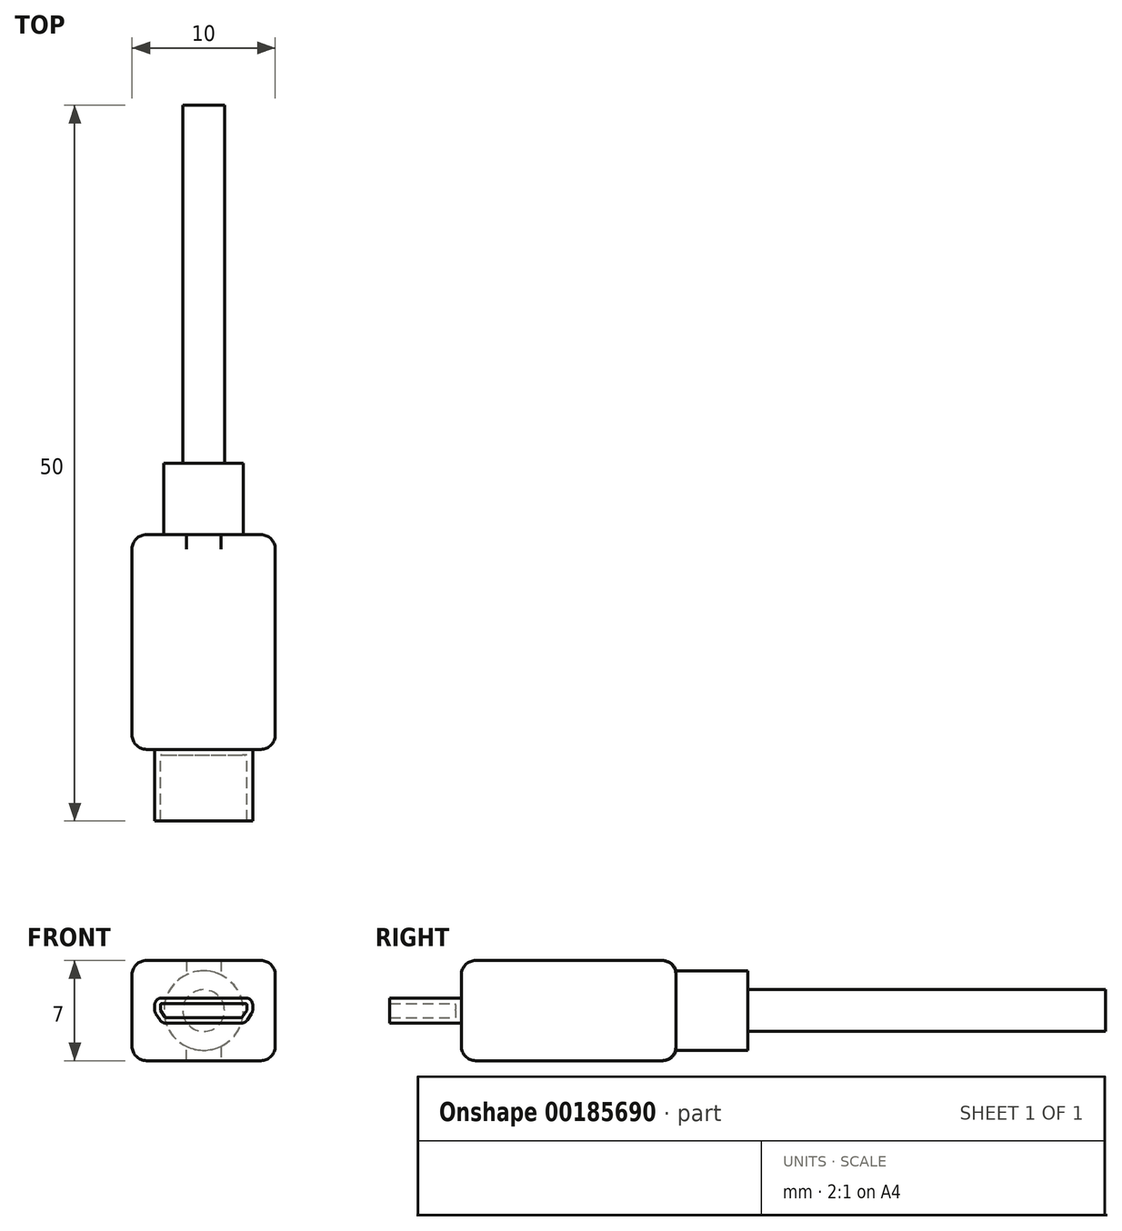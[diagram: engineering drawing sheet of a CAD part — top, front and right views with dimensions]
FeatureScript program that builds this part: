
annotation { "Feature Type Name" : "Feature", "Feature Type Description" : "" }
export const myFeature = defineFeature(function(context is Context, id is Id, definition is map)
    precondition{}
    {
        {
            var Q0;
            Q0=qCreatedBy(makeId("Front.planeOp"),FACE);
            var sketch = newSketch(context, id + "F0", { "sketchPlane" : qUnion([Q0])});
            skLineSegment(sketch, "E0.bottom", {"start": v(5, 3.5) * mm, "end": v(-5, 3.5) * mm});
            skLineSegment(sketch, "E0.top", {"start": v(5, -3.5) * mm, "end": v(-5, -3.5) * mm});
            skLineSegment(sketch, "E0.left", {"start": v(5, 3.5) * mm, "end": v(5, -3.5) * mm});
            skLineSegment(sketch, "E0.right", {"start": v(-5, 3.5) * mm, "end": v(-5, -3.5) * mm});
            skPoint(sketch, "E0.middle", {"position": v(0, 0) * mm});
            skSolve(sketch);
        }
        {
            var Q0;
            Q0=qSketchRegion(id+"F0",true);
            extrude(context, id + "F1", {"entities" : qUnion([Q0]), "oppositeDirection" : true, "depth" : 15 * mm});
        }
        {
            var Q0;
            Q0=makeQuery(id+"F1.opExtrude","CAP_FACE",FACE,{"disambiguationData":[OSD([sQuery(id+"F0.wireOp",EDGE,"E0.bottom"),sQuery(id+"F0.wireOp",EDGE,"E0.top"),sQuery(id+"F0.wireOp",EDGE,"E0.left"),sQuery(id+"F0.wireOp",EDGE,"E0.right")])],"isStart":false});
            var sketch = newSketch(context, id + "F2", { "sketchPlane" : qUnion([Q0])});
            skCircle(sketch, "E1", {"center": v(0, 0) * mm, "radius": 2.77 * mm});
            skSolve(sketch);
        }
        {
            var Q0;
            Q0=qSketchRegion(id+"F2",true);
            extrude(context, id + "F3", {"entities" : qUnion([Q0]), "operationType" : NewBodyOperationType.ADD, "depth" : 5 * mm});
        }
        {
            var Q0;
            Q0=makeQuery(id+"F3.opExtrude","CAP_FACE",FACE,{"disambiguationData":[OSD([sQuery(id+"F2.wireOp",EDGE,"E1")])],"isStart":false});
            var sketch = newSketch(context, id + "F4", { "sketchPlane" : qUnion([Q0])});
            skCircle(sketch, "E2", {"center": v(0, 0) * mm, "radius": 1.46 * mm});
            skSolve(sketch);
        }
        {
            var Q0;
            Q0=qSketchRegion(id+"F4",true);
            extrude(context, id + "F5", {"entities" : qUnion([Q0]), "operationType" : NewBodyOperationType.ADD, "depth" : 25 * mm});
        }
        {
            var Q0;
            Q0=makeQuery(id+"F1.opExtrude","SWEPT_EDGE",EDGE,{"disambiguationData":[OSD([sQuery(id+"F0.wireOp",EDGE,"E0.bottom"),sQuery(id+"F0.wireOp",EDGE,"E0.left")])]});
            var Q1;
            Q1=makeQuery(id+"F1.opExtrude","CAP_EDGE",EDGE,{"disambiguationData":[OSD([sQuery(id+"F0.wireOp",EDGE,"E0.bottom")])],"isStart":false});
            var Q2;
            Q2=makeQuery(id+"F1.opExtrude","SWEPT_EDGE",EDGE,{"disambiguationData":[OSD([sQuery(id+"F0.wireOp",EDGE,"E0.bottom"),sQuery(id+"F0.wireOp",EDGE,"E0.right")])]});
            var Q3;
            Q3=makeQuery(id+"F1.opExtrude","SWEPT_EDGE",EDGE,{"disambiguationData":[OSD([sQuery(id+"F0.wireOp",EDGE,"E0.top"),sQuery(id+"F0.wireOp",EDGE,"E0.right")])]});
            var Q4;
            Q4=makeQuery(id+"F1.opExtrude","CAP_EDGE",EDGE,{"disambiguationData":[OSD([sQuery(id+"F0.wireOp",EDGE,"E0.right")])],"isStart":false});
            var Q5;
            Q5=makeQuery(id+"F1.opExtrude","CAP_EDGE",EDGE,{"disambiguationData":[OSD([sQuery(id+"F0.wireOp",EDGE,"E0.left")])],"isStart":false});
            var Q6;
            Q6=makeQuery(id+"F1.opExtrude","CAP_EDGE",EDGE,{"disambiguationData":[OSD([sQuery(id+"F0.wireOp",EDGE,"E0.top")])],"isStart":false});
            var Q7;
            Q7=makeQuery(id+"F1.opExtrude","SWEPT_EDGE",EDGE,{"disambiguationData":[OSD([sQuery(id+"F0.wireOp",EDGE,"E0.top"),sQuery(id+"F0.wireOp",EDGE,"E0.left")])]});
            var Q8;
            Q8=makeQuery(id+"F1.opExtrude","CAP_FACE",FACE,{"disambiguationData":[OSD([sQuery(id+"F0.wireOp",EDGE,"E0.bottom"),sQuery(id+"F0.wireOp",EDGE,"E0.top"),sQuery(id+"F0.wireOp",EDGE,"E0.left"),sQuery(id+"F0.wireOp",EDGE,"E0.right")])],"isStart":true});
            fillet(context, id + "F6", {"entities" : qUnion([Q0, Q1, Q2, Q3, Q4, Q5, Q6, Q7, Q8]), "radius" : 1 * mm, "tangentPropagation" : true, "allowEdgeOverflow" : false});
        }
        {
            var Q0;
            Q0=makeQuery(id+"F1.opExtrude","CAP_FACE",FACE,{"disambiguationData":[OSD([sQuery(id+"F0.wireOp",EDGE,"E0.bottom"),sQuery(id+"F0.wireOp",EDGE,"E0.top"),sQuery(id+"F0.wireOp",EDGE,"E0.left"),sQuery(id+"F0.wireOp",EDGE,"E0.right")])],"isStart":true});
            var sketch = newSketch(context, id + "F7", { "sketchPlane" : qUnion([Q0])});
            skLineSegment(sketch, "E3", {"start": v(0, 0.89) * mm, "end": v(3.43, 0.89) * mm});
            skLineSegment(sketch, "E4", {"start": v(3.43, 0.88) * mm, "end": v(3.43, -0.08) * mm});
            skLineSegment(sketch, "E5", {"start": v(3.43, -0.08) * mm, "end": v(2.9, -0.89) * mm});
            skLineSegment(sketch, "E6", {"start": v(2.9, -0.89) * mm, "end": v(0, -0.89) * mm});
            skLineSegment(sketch, "E7", {"start": v(0, -0.88) * mm, "end": v(0, 0.89) * mm, "construction": true});
            skPoint(sketch, "E8", {"position": v(0, 0) * mm});
            skLineSegment(sketch, "E9.MirrorCS", {"start": v(-3.43, -0.08) * mm, "end": v(-2.9, -0.89) * mm});
            skLineSegment(sketch, "E10.MirrorCS", {"start": v(-2.9, -0.89) * mm, "end": v(0, -0.88) * mm});
            skLineSegment(sketch, "E11.MirrorCS", {"start": v(-2.9, -0.89) * mm, "end": v(-2.9, -0.89) * mm});
            skLineSegment(sketch, "E12.MirrorCS", {"start": v(0, 0.89) * mm, "end": v(-3.43, 0.88) * mm});
            skLineSegment(sketch, "E13.MirrorCS", {"start": v(-3.43, 0.88) * mm, "end": v(-3.42, -0.08) * mm});
            skSolve(sketch);
        }
        {
            var Q0;
            Q0=qSketchRegion(id+"F7",true);
            extrude(context, id + "F8", {"entities" : qUnion([Q0]), "depth" : 5 * mm});
        }
        {
            var Q0;
            Q0=makeQuery(id+"F8.opExtrude","SWEPT_EDGE",EDGE,{"disambiguationData":[OSD([sQuery(id+"F7.wireOp",EDGE,"E12.MirrorCS"),sQuery(id+"F7.wireOp",EDGE,"E13.MirrorCS")])]});
            var Q1;
            Q1=makeQuery(id+"F8.opExtrude","SWEPT_EDGE",EDGE,{"disambiguationData":[OSD([sQuery(id+"F7.wireOp",EDGE,"E3"),sQuery(id+"F7.wireOp",EDGE,"E4")])]});
            var Q2;
            Q2=makeQuery(id+"F8.opExtrude","SWEPT_EDGE",EDGE,{"disambiguationData":[OSD([sQuery(id+"F7.wireOp",EDGE,"E4"),sQuery(id+"F7.wireOp",EDGE,"E5")])]});
            var Q3;
            Q3=makeQuery(id+"F8.opExtrude","SWEPT_EDGE",EDGE,{"disambiguationData":[OSD([sQuery(id+"F7.wireOp",EDGE,"E5"),sQuery(id+"F7.wireOp",EDGE,"YMRPezVj-6pw8-9NHr-ek3B-FgzowQ8j5mIN")])]});
            var Q4;
            Q4=makeQuery(id+"F8.opExtrude","SWEPT_EDGE",EDGE,{"disambiguationData":[OSD([sQuery(id+"F7.wireOp",EDGE,"YMRPezVj-6pw8-9NHr-ek3B-FgzowQ8j5mIN"),sQuery(id+"F7.wireOp",EDGE,"E6")])]});
            var Q5;
            Q5=makeQuery(id+"F8.opExtrude","SWEPT_EDGE",EDGE,{"disambiguationData":[OSD([sQuery(id+"F7.wireOp",EDGE,"E10.MirrorCS"),sQuery(id+"F7.wireOp",EDGE,"E11.MirrorCS")])]});
            var Q6;
            Q6=makeQuery(id+"F8.opExtrude","SWEPT_EDGE",EDGE,{"disambiguationData":[OSD([sQuery(id+"F7.wireOp",EDGE,"E9.MirrorCS"),sQuery(id+"F7.wireOp",EDGE,"E11.MirrorCS")])]});
            var Q7;
            Q7=makeQuery(id+"F8.opExtrude","SWEPT_EDGE",EDGE,{"disambiguationData":[OSD([sQuery(id+"F7.wireOp",EDGE,"E9.MirrorCS"),sQuery(id+"F7.wireOp",EDGE,"E13.MirrorCS")])]});
            fillet(context, id + "F9", {"entities" : qUnion([Q0, Q1, Q2, Q3, Q4, Q5, Q6, Q7]), "radius" : 0.5 * mm, "tangentPropagation" : true, "allowEdgeOverflow" : false});
        }
        {
            var Q0;
            Q0=makeQuery(id+"F8.opExtrude","CAP_FACE",FACE,{"disambiguationData":[OSD([sQuery(id+"F7.wireOp",EDGE,"E3"),sQuery(id+"F7.wireOp",EDGE,"E4"),sQuery(id+"F7.wireOp",EDGE,"E5"),sQuery(id+"F7.wireOp",EDGE,"YMRPezVj-6pw8-9NHr-ek3B-FgzowQ8j5mIN"),sQuery(id+"F7.wireOp",EDGE,"E6"),sQuery(id+"F7.wireOp",EDGE,"E9.MirrorCS"),sQuery(id+"F7.wireOp",EDGE,"E10.MirrorCS"),sQuery(id+"F7.wireOp",EDGE,"E11.MirrorCS"),sQuery(id+"F7.wireOp",EDGE,"E12.MirrorCS"),sQuery(id+"F7.wireOp",EDGE,"E13.MirrorCS")])],"isStart":false});
            shell(context, id + "F10", {"entities" : qUnion([Q0]), "thickness" : 0.4 * mm});
        }
    });
